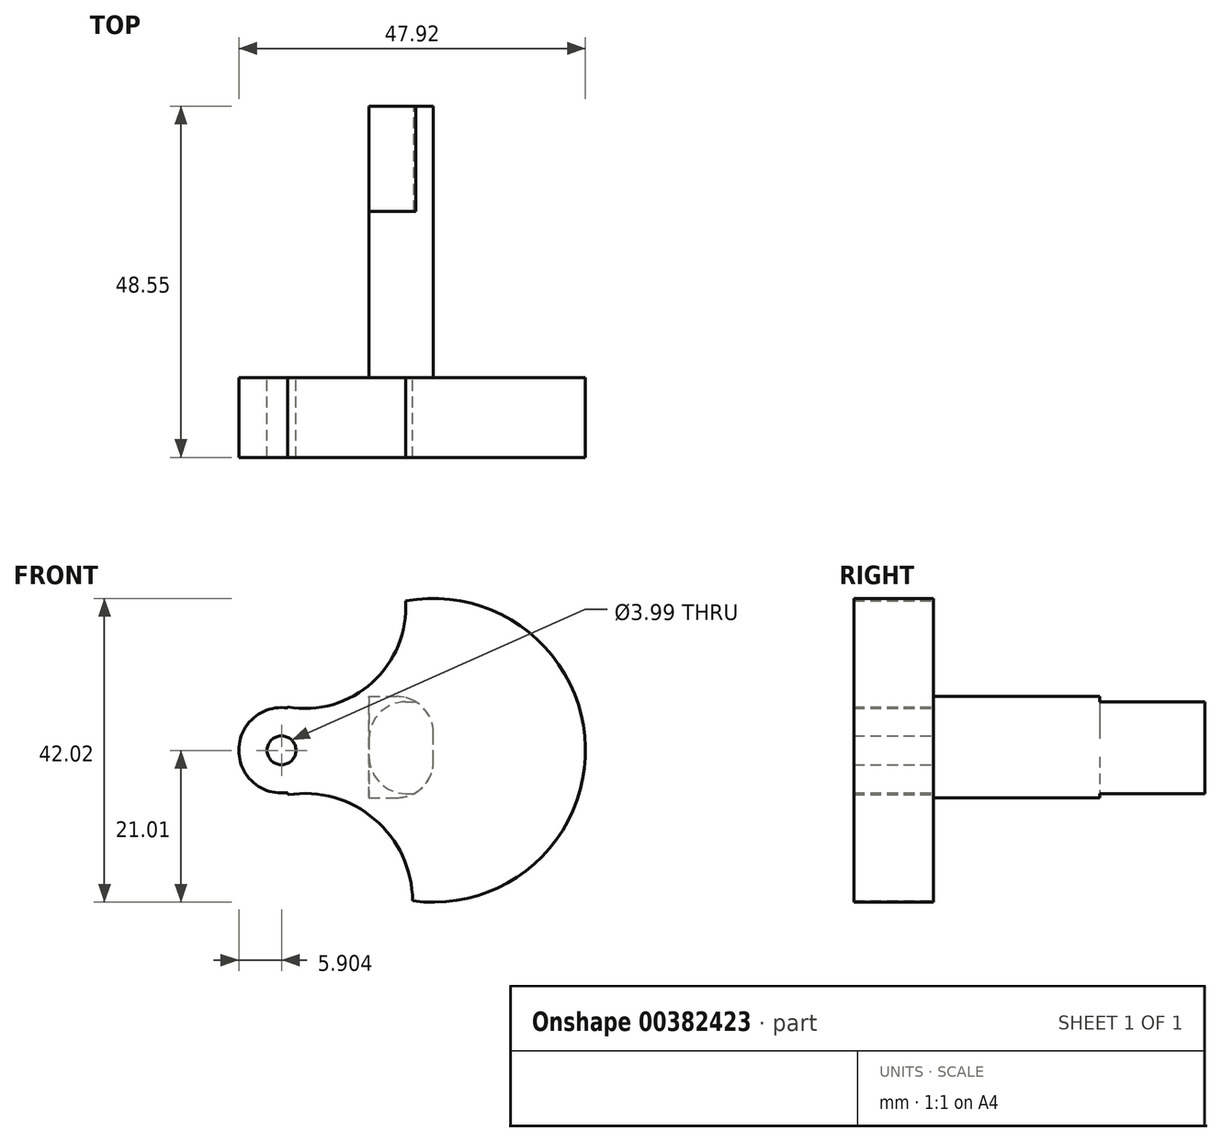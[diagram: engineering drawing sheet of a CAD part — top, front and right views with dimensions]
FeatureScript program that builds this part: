
annotation { "Feature Type Name" : "Feature", "Feature Type Description" : "" }
export const myFeature = defineFeature(function(context is Context, id is Id, definition is map)
    precondition{}
    {
        {
            var Q0;
            Q0=qCreatedBy(makeId("Front.planeOp"),FACE);
            var sketch = newSketch(context, id + "F0", { "sketchPlane" : qUnion([Q0])});
            skArc(sketch, "E0", {"start": v(-20.18, 5.85) * mm, "mid": v(-26.91, 0) * mm, "end": v(-20.18, -5.85) * mm});
            skArc(sketch, "E1", {"start": v(-20.13, 5.99) * mm, "mid": v(-20.16, 5.92) * mm, "end": v(-20.18, 5.85) * mm});
            skArc(sketch, "E2", {"start": v(-2.89, -20.8) * mm, "mid": v(-8.13, -9.53) * mm, "end": v(-20.09, -6.14) * mm});
            skArc(sketch, "E3", {"start": v(-20.13, 5.99) * mm, "mid": v(-8.45, 9.38) * mm, "end": v(-3.84, 20.65) * mm});
            skArc(sketch, "E4.trimOffspring", {"start": v(-2.89, -20.8) * mm, "mid": v(21, 0.48) * mm, "end": v(-3.84, 20.65) * mm});
            skArc(sketch, "E5.trimOffspring", {"start": v(-20.18, -5.85) * mm, "mid": v(-20.13, -6) * mm, "end": v(-20.09, -6.14) * mm});
            skCircle(sketch, "E6", {"center": v(-21, 0) * mm, "radius": 2 * mm});
            skSolve(sketch);
        }
        {
            var Q0;
            Q0 = qSketchRegion(id + "F0", true);
            extrude(context, id + "F1", {"entities" : qUnion([Q0]), "depth" : 11 * mm});
        }
        {
            var Q0;
            Q0=qCreatedBy(makeId("Right.planeOp"),FACE);
            var sketch = newSketch(context, id + "F2", { "sketchPlane" : qUnion([Q0])});
            skLineSegment(sketch, "E7", {"start": v(0, -6.56) * mm, "end": v(0, 7.44) * mm});
            skLineSegment(sketch, "E8", {"start": v(0, 7.44) * mm, "end": v(23.01, 7.44) * mm});
            skLineSegment(sketch, "E9", {"start": v(23.01, 7.44) * mm, "end": v(23.01, -6.56) * mm});
            skLineSegment(sketch, "E10", {"start": v(23.01, -6.56) * mm, "end": v(0, -6.56) * mm});
            skLineSegment(sketch, "E11", {"start": v(23.01, -5.97) * mm, "end": v(37.55, -5.97) * mm});
            skLineSegment(sketch, "E12", {"start": v(23.01, 6.7) * mm, "end": v(37.55, 6.7) * mm});
            skLineSegment(sketch, "E13", {"start": v(37.55, 6.7) * mm, "end": v(37.55, -5.97) * mm});
            skSolve(sketch);
        }
        {
            var Q0;
            Q0 = qSketchRegion(id + "F2", true);
            extrude(context, id + "F3", {"entities" : qUnion([Q0]), "operationType" : NewBodyOperationType.ADD, "oppositeDirection" : true, "depth" : 8.9 * mm});
        }
        {
            var Q0;
            Q0=makeQuery(id+"F3.opExtrude","CAP_EDGE",EDGE,{"disambiguationData":[OSD([sQuery(id+"F2.wireOp",EDGE,"E8")])],"isStart":true});
            var Q1;
            Q1=makeQuery(id+"F3.opExtrude","CAP_EDGE",EDGE,{"disambiguationData":[OSD([sQuery(id+"F2.wireOp",EDGE,"E10")])],"isStart":true});
            var Q2;
            Q2=makeQuery(id+"F3.opExtrude","CAP_EDGE",EDGE,{"disambiguationData":[OSD([sQuery(id+"F2.wireOp",EDGE,"E12")])],"isStart":false});
            var Q3;
            Q3=makeQuery(id+"F3.opExtrude","CAP_EDGE",EDGE,{"disambiguationData":[OSD([sQuery(id+"F2.wireOp",EDGE,"E11")])],"isStart":false});
            fillet(context, id + "F4", {"entities" : qUnion([Q0, Q1, Q2, Q3]), "radius" : 5.08 * mm, "tangentPropagation" : true, "allowEdgeOverflow" : false});
        }
    });
